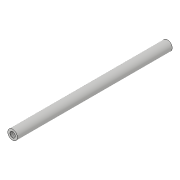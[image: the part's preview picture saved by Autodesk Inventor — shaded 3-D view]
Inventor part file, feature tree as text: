
AUTODESK INVENTOR PART (.ipt)
format: ipt  version: 2018.3 (Build 223284000, 284)  size: 82,944 bytes
history: native  units: in
note: dims shown in document units (in); Inventor stores cm internally (conversion verified against a paired STEP export)
features: sketch x3, hole x2, extrude x1
ambient origin geometry x8: Origin, YZ Plane, XZ Plane, XY Plane, X Axis, Y Axis, Z Axis, Center Point
bodies: Solid1 (feature_tree)
feature tree (6):
  extrude  "Extrusion1"  Depth=3.0in TaperAngle=0.0deg
  hole  "Hole1"  [1 undecoded]
  hole  "Hole2"  [1 undecoded]
  sketch  "Sketch1"  dims[d0=0.1875in d1=3.0in d2=0.0in]
  sketch  "Sketch2"  dims[d3=0.089in]
  sketch  "Sketch3"  dims[d4=0.104in d5=0.276in d6=0.375in d7=0.25in d8=0.5635in d9=0.432in d10=0.8108in d11=0.104in d12=0.276in d13=0.375in d14=0.25in d15=0.5635in d16=0.432in d17=0.8108in]
note: 2 required parameter values undecoded (feature->parameter linkage not recoverable at this tier; creation-order binding heuristic only, values carry confidence <= 0.55)
